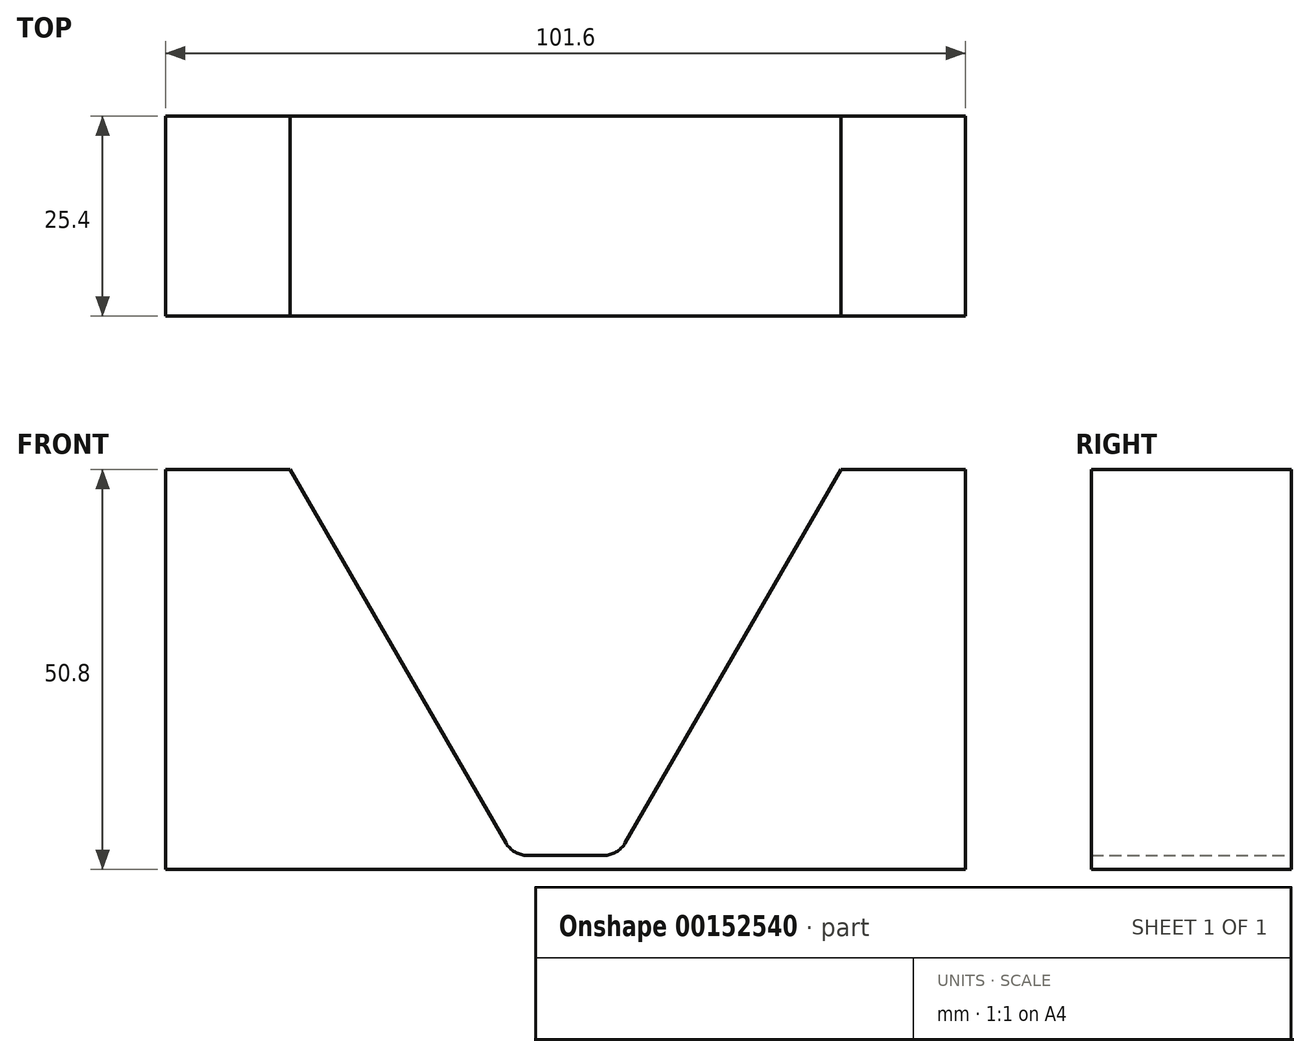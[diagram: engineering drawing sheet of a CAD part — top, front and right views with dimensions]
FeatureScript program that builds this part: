
annotation { "Feature Type Name" : "Feature", "Feature Type Description" : "" }
export const myFeature = defineFeature(function(context is Context, id is Id, definition is map)
    precondition{}
    {
        {
            var Q0;
            Q0=qCreatedBy(makeId("Front.planeOp"),FACE);
            var sketch = newSketch(context, id + "F0", { "sketchPlane" : qUnion([Q0])});
            skLineSegment(sketch, "E0", {"start": v(0, 0) * mm, "end": v(-50.8, 0) * mm});
            skLineSegment(sketch, "E1", {"start": v(-50.8, 0) * mm, "end": v(-50.8, 50.8) * mm});
            skLineSegment(sketch, "E2", {"start": v(-50.8, 50.8) * mm, "end": v(-34.96, 50.8) * mm});
            skLineSegment(sketch, "E3", {"start": v(-34.96, 50.8) * mm, "end": v(-7.58, 3.37) * mm});
            skLineSegment(sketch, "E4", {"start": v(-4.83, 1.78) * mm, "end": v(0, 1.78) * mm});
            skLineSegment(sketch, "E5", {"start": v(0, 1.78) * mm, "end": v(0, 0) * mm});
            skArc(sketch, "E6.filletArc", {"start": v(-7.58, 3.37) * mm, "mid": v(-6.41, 2.2) * mm, "end": v(-4.83, 1.78) * mm});
            skSolve(sketch);
        }
        {
            var Q0;
            Q0 = qSketchRegion(id + "F0", true);
            extrude(context, id + "F1", {"entities" : qUnion([Q0]), "depth" : 25.4 * mm});
        }
        {
            var Q0;
            Q0=makeQuery(id+"F1.opExtrude","SWEPT_BODY",BODY,{"disambiguationData":[OSD([sQuery(id+"F0.wireOp",EDGE,"E0"),sQuery(id+"F0.wireOp",EDGE,"E1"),sQuery(id+"F0.wireOp",EDGE,"E2"),sQuery(id+"F0.wireOp",EDGE,"E3"),sQuery(id+"F0.wireOp",EDGE,"E4"),sQuery(id+"F0.wireOp",EDGE,"E5"),sQuery(id+"F0.wireOp",EDGE,"E6.filletArc")])]});
            var Q1;
            Q1=qCreatedBy(makeId("Right.planeOp"),FACE);
            mirror(context, id + "F2", {"operationType" : NewBodyOperationType.ADD, "entities" : qUnion([Q0]), "mirrorPlane" : qUnion([Q1])});
        }
    });
